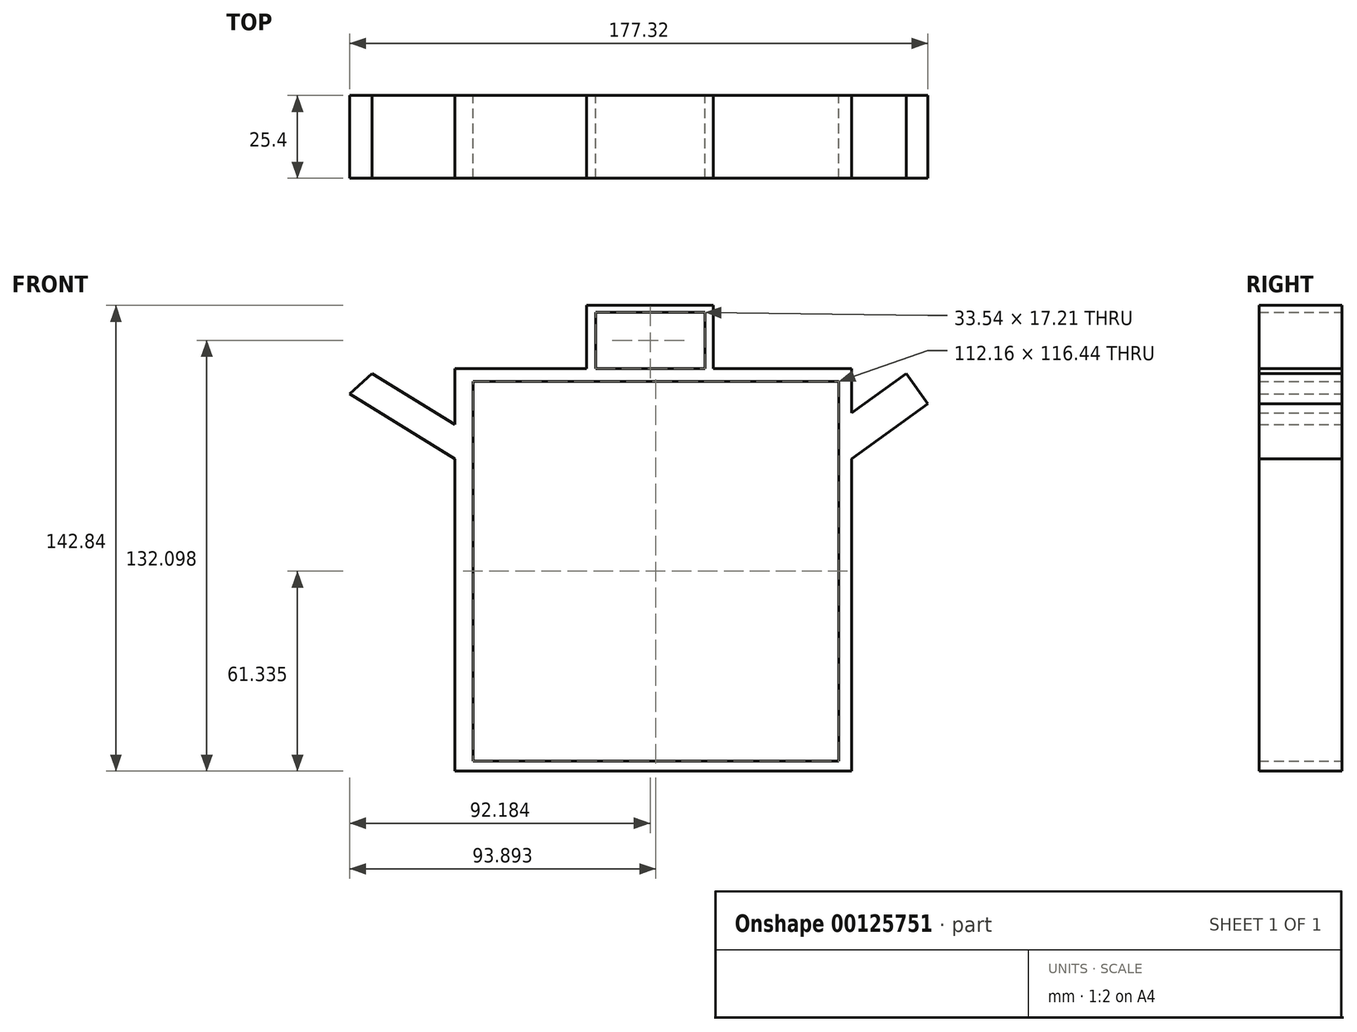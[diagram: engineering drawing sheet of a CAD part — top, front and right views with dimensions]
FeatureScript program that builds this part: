
annotation { "Feature Type Name" : "Feature", "Feature Type Description" : "" }
export const myFeature = defineFeature(function(context is Context, id is Id, definition is map)
    precondition{}
    {
        {
            var Q0;
            Q0=qCreatedBy(makeId("Front.planeOp"),FACE);
            var sketch = newSketch(context, id + "F0", { "sketchPlane" : qUnion([Q0])});
            skLineSegment(sketch, "E0.bottom", {"start": v(-57.2, 56.6) * mm, "end": v(64.48, 56.6) * mm});
            skLineSegment(sketch, "E0.top", {"start": v(-57.2, -66.9) * mm, "end": v(64.48, -66.9) * mm});
            skLineSegment(sketch, "E0.left", {"start": v(-57.2, 56.6) * mm, "end": v(-57.2, -66.9) * mm});
            skLineSegment(sketch, "E0.right", {"start": v(64.48, 56.6) * mm, "end": v(64.48, -66.9) * mm});
            skLineSegment(sketch, "E1", {"start": v(64.48, 28.95) * mm, "end": v(87.87, 45.83) * mm});
            skLineSegment(sketch, "E2", {"start": v(87.87, 45.83) * mm, "end": v(81.21, 55.06) * mm});
            skLineSegment(sketch, "E3", {"start": v(81.21, 55.06) * mm, "end": v(64.48, 42.99) * mm});
            skLineSegment(sketch, "E4", {"start": v(-82.62, 55.06) * mm, "end": v(-89.45, 48.82) * mm});
            skLineSegment(sketch, "E5", {"start": v(-89.45, 48.82) * mm, "end": v(-57.2, 28.95) * mm});
            skLineSegment(sketch, "E6", {"start": v(-82.62, 55.06) * mm, "end": v(-57.2, 39.42) * mm});
            skLineSegment(sketch, "E7.bottom", {"start": v(-51.64, 52.66) * mm, "end": v(60.52, 52.66) * mm});
            skLineSegment(sketch, "E7.top", {"start": v(-51.64, -63.77) * mm, "end": v(60.52, -63.77) * mm});
            skLineSegment(sketch, "E7.left", {"start": v(-51.64, 52.66) * mm, "end": v(-51.64, -63.77) * mm});
            skLineSegment(sketch, "E7.right", {"start": v(60.52, 52.66) * mm, "end": v(60.52, -63.77) * mm});
            skSolve(sketch);
        }
        {
            var Q0;
            {var subQ3=sQuery(id+"F0.wireOp",EDGE,"E0.bottom");Q0=makeQuery(id+"F0.imprint","IMPRINT",FACE,{"disambiguationData":[TD([[makeQuery(id+"F0.imprint","IMPRINT",EDGE,{"derivedFrom":subQ3}),-1.0]])]});}
            var Q1;
            Q1=makeQuery(id+"F0.imprint","IMPRINT",FACE,{"disambiguationData":[TD([[makeQuery(id+"F0.imprint","IMPRINT",EDGE,{"derivedFrom":sQuery(id+"F0.wireOp",EDGE,"E4")}),1.0]])]});
            var Q2;
            {var subQ0=sQuery(id+"F0.wireOp",EDGE,"E1");Q2=makeQuery(id+"F0.imprint","IMPRINT",FACE,{"disambiguationData":[TD([[makeQuery(id+"F0.imprint","IMPRINT",EDGE,{"derivedFrom":subQ0}),1.0]])]});}
            extrude(context, id + "F1", {"entities" : qUnion([Q0, Q1, Q2]), "depth" : 25.4 * mm});
        }
        {
            var Q0;
            Q0=qCreatedBy(makeId("Front.planeOp"),FACE);
            var sketch = newSketch(context, id + "F2", { "sketchPlane" : qUnion([Q0])});
            skLineSegment(sketch, "E8.bottom", {"start": v(-16.82, 52.88) * mm, "end": v(22.07, 52.88) * mm});
            skLineSegment(sketch, "E8.top", {"start": v(-16.82, 75.95) * mm, "end": v(22.07, 75.95) * mm});
            skLineSegment(sketch, "E8.left", {"start": v(-16.82, 52.88) * mm, "end": v(-16.82, 75.95) * mm});
            skLineSegment(sketch, "E8.right", {"start": v(22.07, 52.88) * mm, "end": v(22.07, 75.95) * mm});
            skLineSegment(sketch, "E9.bottom", {"start": v(-14.04, 73.81) * mm, "end": v(19.5, 73.81) * mm});
            skLineSegment(sketch, "E9.top", {"start": v(-14.04, 52.88) * mm, "end": v(19.5, 52.88) * mm});
            skLineSegment(sketch, "E9.left", {"start": v(-14.04, 73.81) * mm, "end": v(-14.04, 52.88) * mm});
            skLineSegment(sketch, "E9.right", {"start": v(19.5, 73.81) * mm, "end": v(19.5, 52.88) * mm});
            skSolve(sketch);
        }
        {
            var Q0;
            Q0=makeQuery(id+"F2.imprint","IMPRINT",FACE,{"disambiguationData":[TD([[makeQuery(id+"F2.imprint","IMPRINT",EDGE,{"derivedFrom":sQuery(id+"F2.wireOp",EDGE,"E8.top")}),-1.0]])]});
            extrude(context, id + "F3", {"entities" : qUnion([Q0]), "operationType" : NewBodyOperationType.ADD, "depth" : 25.4 * mm});
        }
    });
